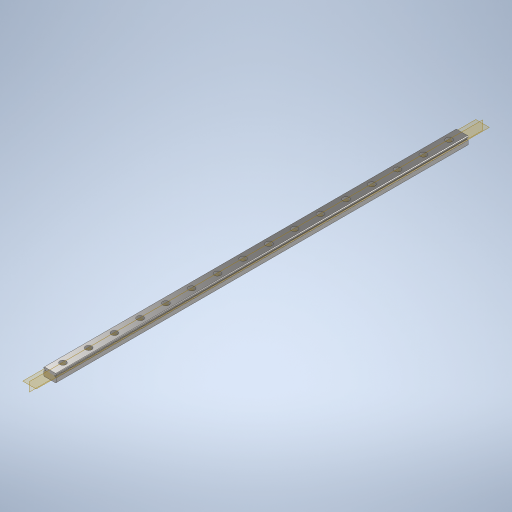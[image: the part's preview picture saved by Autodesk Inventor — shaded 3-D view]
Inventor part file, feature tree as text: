
AUTODESK INVENTOR PART (.ipt)
format: ipt  version: 2024 (Build 280153000, 153)  size: 337,920 bytes
history: native  units: mm
features: pattern_linear x1, plane x1, other x1
ambient origin geometry x8: Origin, YZ Plane, XZ Plane, XY Plane, X Axis, Y Axis, Z Axis, Center Point
bodies: Solid1 (feature_tree)
feature tree (3):
  pattern_linear  "Rectangular Pattern1"  Count1=4  [1 undecoded]
  plane  "Work Plane2"
  other  "LPattern1"
note: 1 required parameter value undecoded (feature->parameter linkage not recoverable at this tier; creation-order binding heuristic only, values carry confidence <= 0.55)
